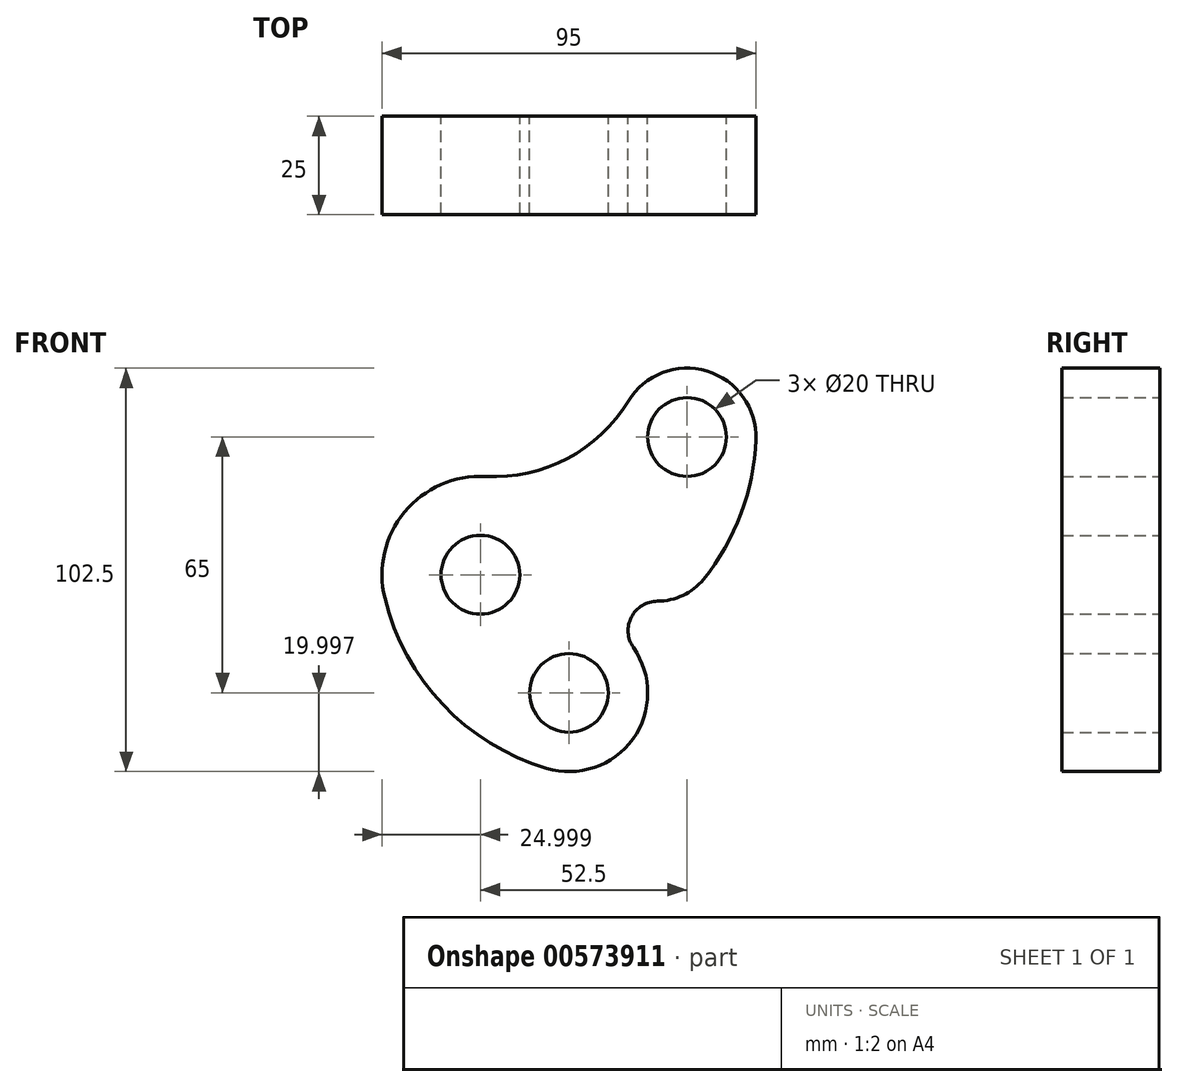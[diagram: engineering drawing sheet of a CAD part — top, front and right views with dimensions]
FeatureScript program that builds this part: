
annotation { "Feature Type Name" : "Feature", "Feature Type Description" : "" }
export const myFeature = defineFeature(function(context is Context, id is Id, definition is map)
    precondition{}
    {
        {
            var Q0;
            Q0=qCreatedBy(makeId("Front.planeOp"),FACE);
            var sketch = newSketch(context, id + "F0", { "sketchPlane" : qUnion([Q0])});
            skCircle(sketch, "E0", {"center": v(-16.75, -3.97) * mm, "radius": 10 * mm});
            skCircle(sketch, "E1", {"center": v(35.75, 31.03) * mm, "radius": 10 * mm});
            skCircle(sketch, "E2", {"center": v(5.75, -33.97) * mm, "radius": 10 * mm});
            skArc(sketch, "E3", {"start": v(-15.45, 21) * mm, "mid": v(-36, 11.97) * mm, "end": v(-41.04, -9.9) * mm});
            skArc(sketch, "E4", {"start": v(53.24, 30.36) * mm, "mid": v(40.8, 47.78) * mm, "end": v(20.8, 40.13) * mm});
            skArc(sketch, "E5", {"start": v(0, -53.13) * mm, "mid": v(21.97, -45.68) * mm, "end": v(22.12, -22.48) * mm});
            skArc(sketch, "E6", {"start": v(-41.04, -9.9) * mm, "mid": v(-26.26, -36.97) * mm, "end": v(0, -53.13) * mm});
            skArc(sketch, "E7", {"start": v(-15.45, 21) * mm, "mid": v(5.32, 25.57) * mm, "end": v(20.8, 40.13) * mm});
            skArc(sketch, "E8", {"start": v(28.26, -10.67) * mm, "mid": v(34.7, -9.21) * mm, "end": v(39.9, -5.11) * mm});
            skArc(sketch, "E9", {"start": v(39.9, -5.11) * mm, "mid": v(49.45, 11.54) * mm, "end": v(53.24, 30.36) * mm});
            skArc(sketch, "E10", {"start": v(28.26, -10.67) * mm, "mid": v(21.6, -14.72) * mm, "end": v(22.12, -22.48) * mm});
            skSolve(sketch);
        }
        {
            var Q0;
            Q0=makeQuery(id+"F0.imprint","IMPRINT",FACE,{"disambiguationData":[TD([[makeQuery(id+"F0.imprint","IMPRINT",EDGE,{"derivedFrom":sQuery(id+"F0.wireOp",EDGE,"E0")}),-1.0]])]});
            extrude(context, id + "F1", {"entities" : qUnion([Q0]), "depth" : 25 * mm, "offsetDistance" : 25 * mm});
        }
    });
